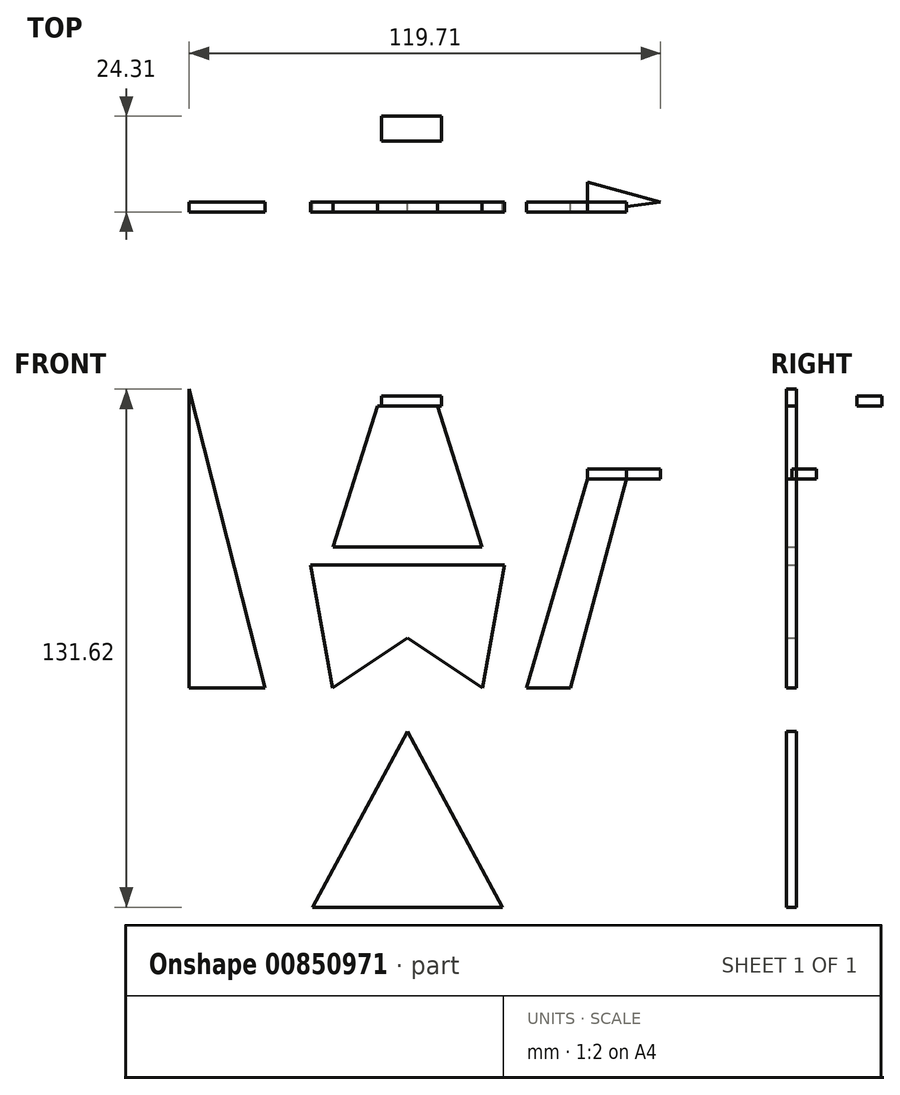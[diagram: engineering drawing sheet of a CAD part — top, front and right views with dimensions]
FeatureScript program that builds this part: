
annotation { "Feature Type Name" : "Feature", "Feature Type Description" : "" }
export const myFeature = defineFeature(function(context is Context, id is Id, definition is map)
    precondition{}
    {
        {
            var Q0;
            Q0=qCreatedBy(makeId("Front.planeOp"),FACE);
            var sketch = newSketch(context, id + "F0", { "sketchPlane" : qUnion([Q0])});
            skLineSegment(sketch, "E0", {"start": v(0, 12.71) * mm, "end": v(-19, 0) * mm});
            skLineSegment(sketch, "E1", {"start": v(0, 12.71) * mm, "end": v(19, 0) * mm});
            skLineSegment(sketch, "E2", {"start": v(-19, 0) * mm, "end": v(-24.63, 31.25) * mm});
            skLineSegment(sketch, "E3", {"start": v(-24.63, 31.25) * mm, "end": v(24.63, 31.25) * mm});
            skLineSegment(sketch, "E4", {"start": v(19, 0) * mm, "end": v(24.63, 31.25) * mm});
            skSolve(sketch);
        }
        {
            var Q0;
            Q0=makeQuery(id+"F0.imprint","IMPRINT",FACE,{"disambiguationData":[TD([[makeQuery(id+"F0.imprint","IMPRINT",EDGE,{"derivedFrom":sQuery(id+"F0.wireOp",EDGE,"E0")}),-1.0]])]});
            extrude(context, id + "F1", {"entities" : qUnion([Q0]), "depth" : 2.54 * mm, "offsetDistance" : 25.4 * mm});
        }
        {
            var Q0;
            Q0=qCreatedBy(makeId("Front.planeOp"),FACE);
            var sketch = newSketch(context, id + "F2", { "sketchPlane" : qUnion([Q0])});
            skLineSegment(sketch, "E5", {"start": v(0, -55.73) * mm, "end": v(-24.13, -55.73) * mm});
            skLineSegment(sketch, "E6", {"start": v(0, -55.73) * mm, "end": v(24.13, -55.73) * mm});
            skLineSegment(sketch, "E7", {"start": v(-24.13, -55.73) * mm, "end": v(0, -11.03) * mm});
            skLineSegment(sketch, "E8", {"start": v(0, -11.03) * mm, "end": v(24.13, -55.73) * mm});
            skSolve(sketch);
        }
        {
            var Q0;
            Q0=makeQuery(id+"F2.imprint","IMPRINT",FACE,{"disambiguationData":[TD([[makeQuery(id+"F2.imprint","IMPRINT",EDGE,{"derivedFrom":sQuery(id+"F2.wireOp",EDGE,"E5")}),-1.0]])]});
            extrude(context, id + "F3", {"entities" : qUnion([Q0]), "depth" : 2.54 * mm, "offsetDistance" : 25.4 * mm});
        }
        {
            var Q0;
            Q0=qCreatedBy(makeId("Front.planeOp"),FACE);
            var sketch = newSketch(context, id + "F4", { "sketchPlane" : qUnion([Q0])});
            skLineSegment(sketch, "E9", {"start": v(-18.87, 0) * mm, "end": v(-18.87, 35.76) * mm});
            skLineSegment(sketch, "E10", {"start": v(18.9, 0) * mm, "end": v(18.9, 35.76) * mm});
            skLineSegment(sketch, "E11", {"start": v(-18.87, 35.76) * mm, "end": v(18.9, 35.76) * mm});
            skLineSegment(sketch, "E12", {"start": v(0, 35.76) * mm, "end": v(0, 71.57) * mm});
            skLineSegment(sketch, "E13", {"start": v(0, 71.57) * mm, "end": v(-7.62, 71.57) * mm});
            skLineSegment(sketch, "E14", {"start": v(0, 71.57) * mm, "end": v(7.62, 71.57) * mm});
            skLineSegment(sketch, "E15", {"start": v(-18.87, 35.76) * mm, "end": v(-7.62, 71.57) * mm});
            skLineSegment(sketch, "E16", {"start": v(7.62, 71.57) * mm, "end": v(18.9, 35.76) * mm});
            skSolve(sketch);
        }
        {
            var Q0;
            {var subQ2=sQuery(id+"F4.wireOp",EDGE,"E12");Q0=makeQuery(id+"F4.imprint","IMPRINT",FACE,{"disambiguationData":[TD([[makeQuery(id+"F4.imprint","IMPRINT",EDGE,{"derivedFrom":subQ2}),1.0]])]});}
            var Q1;
            {var subQ2=sQuery(id+"F4.wireOp",EDGE,"E12");Q1=makeQuery(id+"F4.imprint","IMPRINT",FACE,{"disambiguationData":[TD([[makeQuery(id+"F4.imprint","IMPRINT",EDGE,{"derivedFrom":subQ2}),-1.0]])]});}
            extrude(context, id + "F5", {"entities" : qUnion([Q0, Q1]), "depth" : 2.54 * mm, "offsetDistance" : 25.4 * mm});
        }
        {
            var Q0;
            Q0=makeQuery(id+"F5.opExtrude","SWEPT_FACE",FACE,{"disambiguationData":[OSD([sQuery(id+"F4.wireOp",EDGE,"E13"),sQuery(id+"F4.wireOp",EDGE,"E14")])]});
            var sketch = newSketch(context, id + "F6", { "sketchPlane" : qUnion([Q0])});
            skLineSegment(sketch, "E17", {"start": v(-6.57, 15.42) * mm, "end": v(8.67, 15.42) * mm});
            skLineSegment(sketch, "E18", {"start": v(-6.57, 15.42) * mm, "end": v(-6.57, 21.77) * mm});
            skLineSegment(sketch, "E19", {"start": v(8.67, 15.42) * mm, "end": v(8.67, 21.77) * mm});
            skLineSegment(sketch, "E20", {"start": v(-6.57, 21.77) * mm, "end": v(8.67, 21.77) * mm});
            skSolve(sketch);
        }
        {
            var Q0;
            Q0=makeQuery(id+"F6.imprint","IMPRINT",FACE,{"disambiguationData":[TD([[makeQuery(id+"F6.imprint","IMPRINT",EDGE,{"derivedFrom":sQuery(id+"F6.wireOp",EDGE,"E17")}),1.0]])]});
            extrude(context, id + "F7", {"entities" : qUnion([Q0]), "depth" : 2.54 * mm, "offsetDistance" : 25.4 * mm});
        }
        {
            var Q0;
            Q0=qCreatedBy(makeId("Front.planeOp"),FACE);
            var sketch = newSketch(context, id + "F8", { "sketchPlane" : qUnion([Q0])});
            skLineSegment(sketch, "E21", {"start": v(30.17, 0) * mm, "end": v(45.77, 53.03) * mm});
            skLineSegment(sketch, "E22", {"start": v(45.77, 53.03) * mm, "end": v(55.6, 53.03) * mm});
            skLineSegment(sketch, "E23", {"start": v(55.6, 53.03) * mm, "end": v(41.44, 0) * mm});
            skLineSegment(sketch, "E24", {"start": v(41.44, 0) * mm, "end": v(30.17, 0) * mm});
            skSolve(sketch);
        }
        {
            var Q0;
            Q0=makeQuery(id+"F8.imprint","IMPRINT",FACE,{"disambiguationData":[TD([[makeQuery(id+"F8.imprint","IMPRINT",EDGE,{"derivedFrom":sQuery(id+"F8.wireOp",EDGE,"E21")}),-1.0]])]});
            extrude(context, id + "F9", {"entities" : qUnion([Q0]), "depth" : 2.54 * mm, "offsetDistance" : 25.4 * mm});
        }
        {
            var Q0;
            Q0=makeQuery(id+"F9.opExtrude","SWEPT_FACE",FACE,{"disambiguationData":[OSD([sQuery(id+"F8.wireOp",EDGE,"E22")])]});
            var sketch = newSketch(context, id + "F10", { "sketchPlane" : qUnion([Q0])});
            skLineSegment(sketch, "E25", {"start": v(45.77, -2.54) * mm, "end": v(45.77, 5.08) * mm});
            skLineSegment(sketch, "E26", {"start": v(45.77, 5.08) * mm, "end": v(64.28, 0) * mm});
            skLineSegment(sketch, "E27", {"start": v(64.28, 0) * mm, "end": v(45.77, -2.54) * mm});
            skSolve(sketch);
        }
        {
            var Q0;
            {var subQ1=sQuery(id+"F10.wireOp",EDGE,"E26");Q0=makeQuery(id+"F10.imprint","IMPRINT",FACE,{"disambiguationData":[TD([[makeQuery(id+"F10.imprint","IMPRINT",EDGE,{"derivedFrom":subQ1}),-1.0]])]});}
            extrude(context, id + "F11", {"entities" : qUnion([Q0]), "depth" : 2.54 * mm, "offsetDistance" : 25.4 * mm});
        }
        {
            var Q0;
            Q0=qCreatedBy(makeId("Front.planeOp"),FACE);
            var sketch = newSketch(context, id + "F12", { "sketchPlane" : qUnion([Q0])});
            skLineSegment(sketch, "E28", {"start": v(-36.19, 0) * mm, "end": v(-55.43, 75.89) * mm});
            skLineSegment(sketch, "E29", {"start": v(-55.43, 75.89) * mm, "end": v(-55.43, 0) * mm});
            skLineSegment(sketch, "E30", {"start": v(-55.43, 0) * mm, "end": v(-36.19, 0) * mm});
            skSolve(sketch);
        }
        {
            var Q0;
            Q0=makeQuery(id+"F12.imprint","IMPRINT",FACE,{"disambiguationData":[TD([[makeQuery(id+"F12.imprint","IMPRINT",EDGE,{"derivedFrom":sQuery(id+"F12.wireOp",EDGE,"E28")}),1.0]])]});
            extrude(context, id + "F13", {"entities" : qUnion([Q0]), "depth" : 2.54 * mm, "offsetDistance" : 25.4 * mm});
        }
    });
